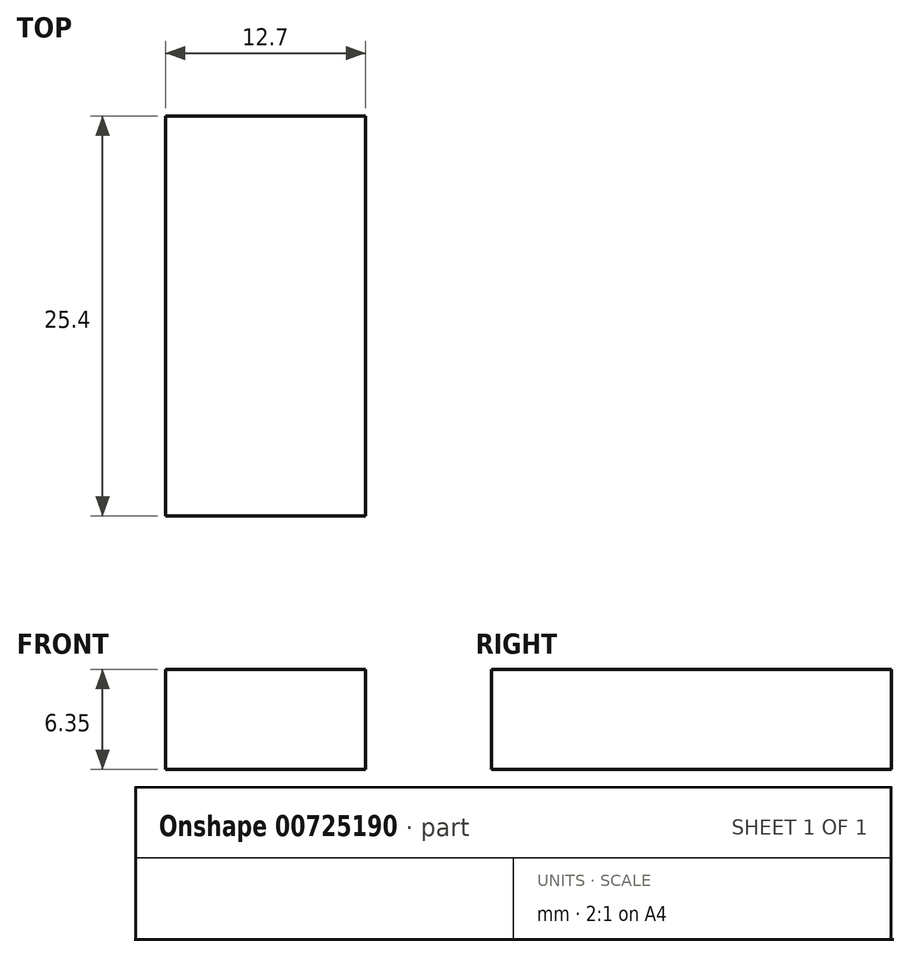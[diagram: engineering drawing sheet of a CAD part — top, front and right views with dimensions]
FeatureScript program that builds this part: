
annotation { "Feature Type Name" : "Feature", "Feature Type Description" : "" }
export const myFeature = defineFeature(function(context is Context, id is Id, definition is map)
    precondition{}
    {
        {
            var Q0;
            Q0=qCreatedBy(makeId("Front.planeOp"),FACE);
            var sketch = newSketch(context, id + "F0", { "sketchPlane" : qUnion([Q0])});
            skLineSegment(sketch, "E0.bottom", {"start": v(0, 0) * mm, "end": v(12.7, 0) * mm});
            skLineSegment(sketch, "E0.top", {"start": v(0, -6.35) * mm, "end": v(12.7, -6.35) * mm});
            skLineSegment(sketch, "E0.left", {"start": v(0, 0) * mm, "end": v(0, -6.35) * mm});
            skLineSegment(sketch, "E0.right", {"start": v(12.7, 0) * mm, "end": v(12.7, -6.35) * mm});
            skSolve(sketch);
        }
        {
            var Q0;
            Q0 = qSketchRegion(id + "F0", true);
            extrude(context, id + "F1", {"entities" : qUnion([Q0]), "depth" : 25.4 * mm, "offsetDistance" : 25.4 * mm});
        }
    });
